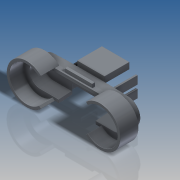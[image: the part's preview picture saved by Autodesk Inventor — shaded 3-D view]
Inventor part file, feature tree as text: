
AUTODESK INVENTOR PART (.ipt)
format: ipt  version: 2016 SP2 (Build 200236200, 236)  size: 686,592 bytes
history: native  units: in
note: dims shown in document units (in); Inventor stores cm internally (conversion verified against a paired STEP export)
features: extrude x8, sketch x7, plane x2, loft x2, fillet x1, projected_geometry x1
ambient origin geometry x8: Origin, YZ Plane, XZ Plane, XY Plane, X Axis, Y Axis, Z Axis, Center Point
bodies: Body1 (feature_tree)
feature tree (21):
  sketch  "Sketch2"  dims[d0=0.056in d1=1.2598in d2=0.378in]
  sketch  "Sketch3"  dims[d3=0.6299in d6=0.5984in]
  plane  "Work Plane2"
  sketch  "Sketch5"  dims[d7=0.6929in d8=0.2362in]
  plane  "Work Plane3"
  sketch  "Sketch6"  dims[d9=0.0787in d10=0.2292in]
  loft  "Loft1"
  loft  "Loft2"
  extrude  "Extrusion3"  Depth=0.2362in
  extrude  "Extrusion4"  Depth=0.2292in
  extrude  "Extrusion5"  Depth=0.056in
  sketch  "Sketch8"  dims[d23=0.4724in d24=0.4409in]
  extrude  "Extrusion6"  Depth=0.4409in
  extrude  "Extrusion7"  TaperAngle=0.0deg  [1 undecoded]
  extrude  "Extrusion8"  TaperAngle=0.0deg  [1 undecoded]
  extrude  "Extrusion9"  TaperAngle=0.0deg  [1 undecoded]
  extrude  "Extrusion10"  Depth=0.0039in
  fillet  "Fillet1"  Radius=0.4724in
  sketch  "Sketch7"  dims[d12=0.6465in d13=0.056in]
  sketch  "Sketch9"  dims[d25=0.0in d26=90.0deg d27=0.0in d28=90.0deg d29=0.0in d30=90.0deg d31=0.0in d32=90.0deg d34=0.0472in d35=0.4724in d36=0.2362in d37=0.0in d38=0.0787in d39=0.0in d40=0.0236in d41=0.063in d42=0.0in d43=0.182in d44=0.3465in d45=0.0315in d46=0.6614in d47=0.4724in d48=0.1102in d49=0.0472in d50=0.315in d51=0.0157in d52=0.0in d53=0.4252in d54=0.0in d55=0.0472in d56=0.0in d57=0.4409in d58=0.0in d59=0.063in d60=0.2835in d61=0.4409in d62=0.0in d63=0.0039in]
  projected_geometry  "Projected Loop1"
note: 3 required parameter values undecoded (feature->parameter linkage not recoverable at this tier; creation-order binding heuristic only, values carry confidence <= 0.55)
